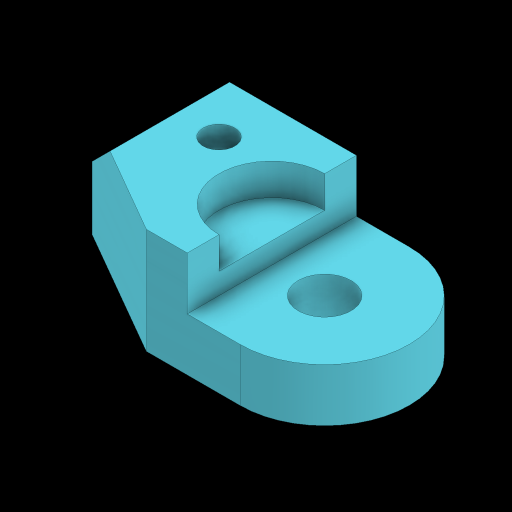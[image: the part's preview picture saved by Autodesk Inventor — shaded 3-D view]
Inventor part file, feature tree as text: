
AUTODESK INVENTOR PART (.ipt)
format: ipt  version: 2024 (Build 280153000, 153)  size: 159,744 bytes
history: native  units: in
note: dims shown in document units (in); Inventor stores cm internally (conversion verified against a paired STEP export)
features: extrude x3, sketch x3, chamfer x1
ambient origin geometry x8: Origin, YZ Plane, XZ Plane, XY Plane, X Axis, Y Axis, Z Axis, Center Point
bodies: Solid1 (feature_tree)
feature tree (7):
  extrude  "MAIN BLOCK"  Depth=5.25in
  extrude  "SQUARE CUTOUT"  Depth=2.25in
  extrude  "HALF CIRCLE CUTOUT"  Depth=0.75in
  chamfer  "REAR CHAMFER"  Distance=1.25in
  sketch  "Sketch1"  dims[d0=4.0in d1=5.25in]
  sketch  "Sketch2"  dims[d4=60.0deg d5=2.25in]
  sketch  "Sketch3"  dims[d6=1.25in d7=0.75in d8=1.25in d9=3.25in d10=2.5in d11=0.0in d12=1.25in d13=1.25in d14=0.0in d15=2.5in d16=0.75in d17=0.0in d18=1.0in d19=0.125in d20=45.0deg]
